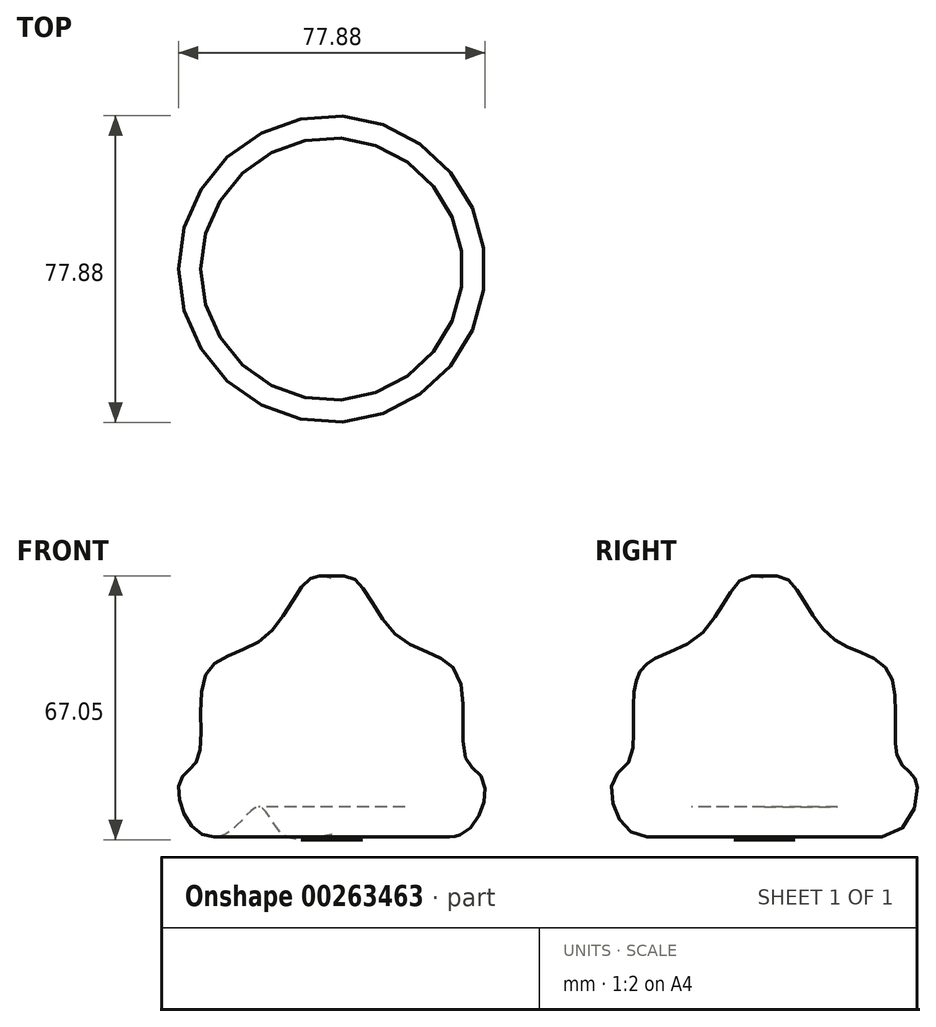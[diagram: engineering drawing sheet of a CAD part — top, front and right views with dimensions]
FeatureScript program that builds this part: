
annotation { "Feature Type Name" : "Feature", "Feature Type Description" : "" }
export const myFeature = defineFeature(function(context is Context, id is Id, definition is map)
    precondition{}
    {
        {
            var Q0;
            Q0=qCreatedBy(makeId("Front.planeOp"),FACE);
            var sketch = newSketch(context, id + "F0", { "sketchPlane" : qUnion([Q0])});
            skLineSegment(sketch, "E0", {"start": v(0, 0) * mm, "end": v(0, 78.63) * mm, "construction": true});
            skSolve(sketch);
        }
        {
            var Q0;
            Q0=qCreatedBy(makeId("Front.planeOp"),FACE);
            var sketch = newSketch(context, id + "F1", { "sketchPlane" : qUnion([Q0])});
            skFitSpline(sketch, "E1", {"points": [v(0, 0) * mm, v(-12.42, 0) * mm, v(-18.49, 6.9) * mm, v(-27.04, 0) * mm, v(-36.14, 2.76) * mm, v(-38.35, 14.07) * mm, v(-33.94, 19.31) * mm, v(-31.73, 41.1) * mm, v(-17.1, 49.94) * mm, v(-5.8, 64.84) * mm, v(0, 65.11) * mm], "startDerivative": vector(-137.55, -35.04) * mm, "endDerivative": vector(85.03, -22.67) * mm});
            skSolve(sketch);
        }
        {
            var Q0;
            Q0=sQuery(id+"F1.wireOp",EDGE,"E1");
            var Q1;
            Q1=sQuery(id+"F0.wireOp",EDGE,"E0");
            revolve(context, id + "F2", {"bodyType" : ToolBodyType.SURFACE, "surfaceEntities" : qUnion([Q0]), "axis" : qUnion([Q1]), "revolveType" : RevolveType.FULL});
        }
    });
